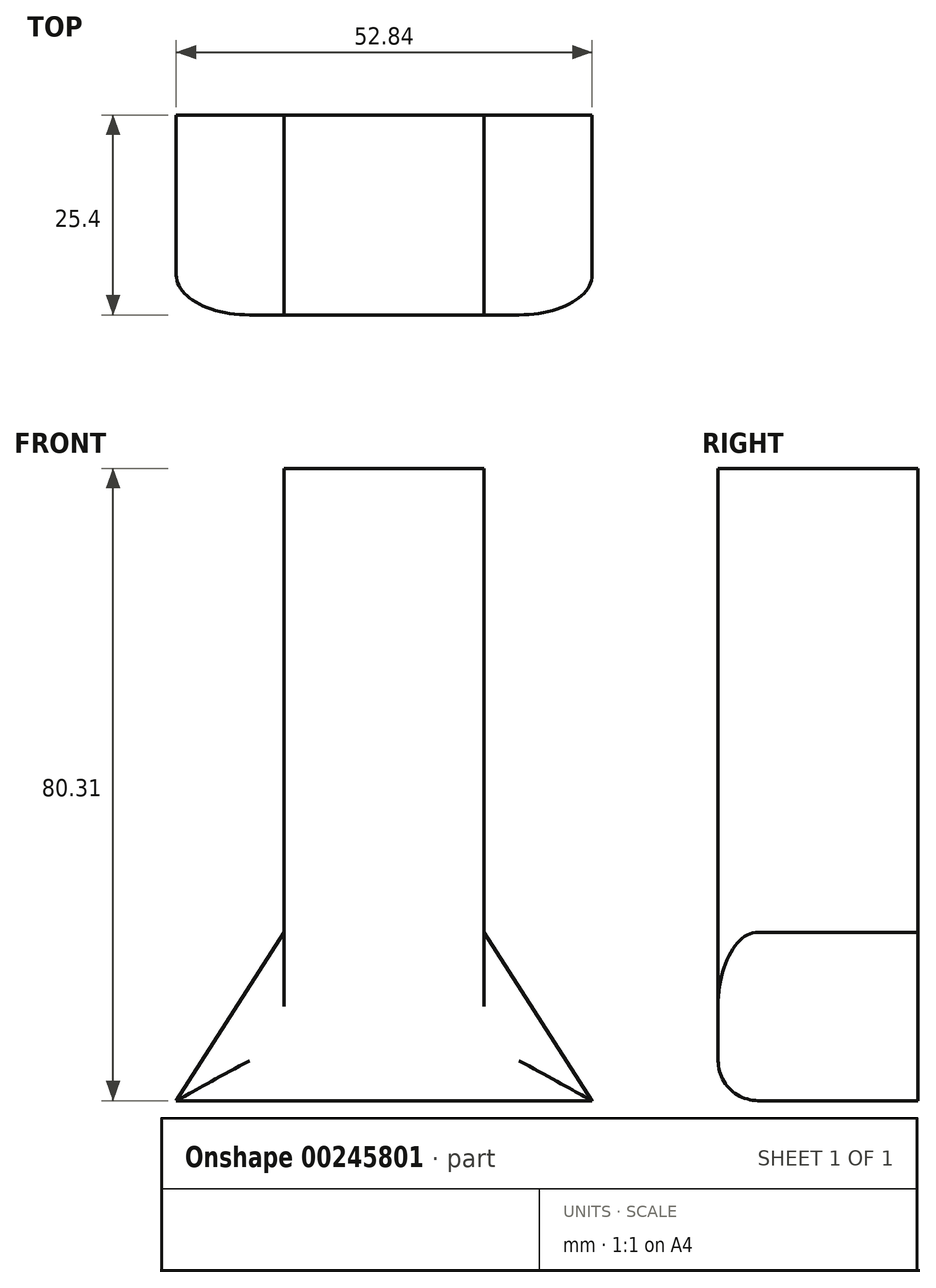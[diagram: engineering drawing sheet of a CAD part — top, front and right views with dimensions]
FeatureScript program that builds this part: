
annotation { "Feature Type Name" : "Feature", "Feature Type Description" : "" }
export const myFeature = defineFeature(function(context is Context, id is Id, definition is map)
    precondition{}
    {
        {
            var Q0;
            Q0=qCreatedBy(makeId("Front.planeOp"),FACE);
            var sketch = newSketch(context, id + "F0", { "sketchPlane" : qUnion([Q0])});
            skLineSegment(sketch, "E0.bottom", {"start": v(-12.62, 58.93) * mm, "end": v(12.78, 58.93) * mm});
            skLineSegment(sketch, "E0.top", {"start": v(-12.62, 0) * mm, "end": v(12.78, 0) * mm});
            skLineSegment(sketch, "E0.left", {"start": v(-12.62, 58.93) * mm, "end": v(-12.62, 0) * mm});
            skLineSegment(sketch, "E0.right", {"start": v(12.78, 58.93) * mm, "end": v(12.78, 0) * mm});
            skLineSegment(sketch, "E1", {"start": v(-12.62, 0) * mm, "end": v(-26.34, -21.38) * mm});
            skLineSegment(sketch, "E2", {"start": v(12.78, 0) * mm, "end": v(26.5, -21.38) * mm});
            skLineSegment(sketch, "E3", {"start": v(-26.34, -21.38) * mm, "end": v(26.5, -21.38) * mm});
            skSolve(sketch);
        }
        {
            var Q0;
            Q0=makeQuery(id+"F0.imprint","IMPRINT",FACE,{"disambiguationData":[TD([[makeQuery(id+"F0.imprint","IMPRINT",EDGE,{"derivedFrom":sQuery(id+"F0.wireOp",EDGE,"E0.bottom")}),-1.0]])]});
            var Q1;
            Q1=makeQuery(id+"F0.imprint","IMPRINT",FACE,{"disambiguationData":[TD([[makeQuery(id+"F0.imprint","IMPRINT",EDGE,{"derivedFrom":sQuery(id+"F0.wireOp",EDGE,"E0.top")}),-1.0]])]});
            extrude(context, id + "F1", {"entities" : qUnion([Q0, Q1]), "depth" : 25.4 * mm});
        }
        {
            var Q0;
            Q0=makeQuery(id+"F1.opExtrude","CAP_EDGE",EDGE,{"disambiguationData":[OSD([sQuery(id+"F0.wireOp",EDGE,"E1")])],"isStart":false});
            var Q1;
            Q1=makeQuery(id+"F1.opExtrude","CAP_EDGE",EDGE,{"disambiguationData":[OSD([sQuery(id+"F0.wireOp",EDGE,"E3")])],"isStart":false});
            var Q2;
            Q2=makeQuery(id+"F1.opExtrude","CAP_EDGE",EDGE,{"disambiguationData":[OSD([sQuery(id+"F0.wireOp",EDGE,"E2")])],"isStart":false});
            fillet(context, id + "F2", {"entities" : qUnion([Q0, Q1, Q2]), "radius" : 5.08 * mm, "tangentPropagation" : true, "allowEdgeOverflow" : false});
        }
    });
